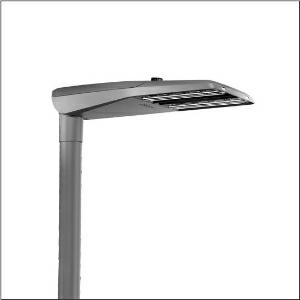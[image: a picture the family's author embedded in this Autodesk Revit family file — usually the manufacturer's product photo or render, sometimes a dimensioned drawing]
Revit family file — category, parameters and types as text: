
# Revit family: streetlight_sl_11_iq_midi___st1_2a_5xc3a41u08le_6743
name_source: partatom
category: Lighting Fixtures
units: mm (PartAtom-declared; Revit-internal decimal feet)

## family parameters
Cut with Voids When Loaded = No
Host = Face
Light Source = No
Part Type = Normal
Room Calculation Point = No
Round Connector Dimension = Use Diameter
Shared = No

## types (1)
- --- (1 x LED, 9590 lm, 59.4 W, 4000K)
    Apparent Load = 59 VA
    CIE Flux Codes = 32 70 96 100 100
    Color Rendering = 70
    Color Temperature = 4000K
    Default Elevation = 1800 mm
    Description = Streetlight SL 11 iQ midi, mast luminaire, primary light control with 3 zone facetted reflector, of plastic, silver coated, highly specular, primary optical cover: cover, of PMMA, transparent, light distribution: ST1.2a, light emission: direct distribution, primary light characteristic: asymmetric, installation type: post-top, side-entry, lamps: LED, High Power LED, rated values: 9.590lm | 59,4W | 161,4lm/W (begin service life); end service life: 9.590lm | 61,6W; at 50% lumin. flux: 4.795lm | 28,5W | 168,2lm/W, colour temperature: 4000K, colour rendering: CRI > 70, light colour: 740, light setting 1 begin service life: 100% | 9.590lm | 59,4W | 161,4lm/W | 4.000K, light setting 1 end service life: 61,6W, further light settings possible, control: pre-setting: logarithmic dimming characteristic, Street-Remote, Auto-Match, Temp-Guard, Lumen-Switch, Night-Set, Smart-Wire, Light-Fading, Desk-Remote (wireless, voltage-free reading and setting of iQ features in the workshop via application-optimized NFC function/RFID function), optimised constant luminous flux control (CLO 2.0), with cable H07RN-F 3x 1.5mm², mains connection: 230..240V, AC, 50/60Hz, connection cable pre-assembled, cable length: 8,5m, luminaire housing, of diecast aluminium, powder-coated, SITECO metallic grey (DB 702S), please order mast flange separately, inclination adjustable without tools: 0°, 5°, 10°, 15° (post-top) | 0°, -5°, -10°, -15° (side-entry), sealing non-destructively replaceable, multi-level sealing system, length: 780mm, width: 376mm, height: 118mm, mast flange for spigot size: 42mm (side-entry): 5XC10008XM4, 60/48mm (side-entry/post-top): 5XC10108XM2, 76/60mm (side-entry/post-top): 5XC10108XM1, equipment: standard, Smart Interface below, protection rating (complete): IP66, insulation class (complete): insulation class II (safety insulation), certification: CE, ENEC, ENEC+, VDE, UKCA, impact resistance: IK10, permissible operating ambient temperature for outdoor applications: -25..+50°C, standard-compliant lighting for roads and squares, Environmental Product Declaration (EPD) tested and certified by an independent institute, packaging unit: 1 piece

Light Distribution: ST1.2a
    Height = 118 mm
    Lamp = 1 x LED
    Lamp Light Flux = 9590 lm
    Lamp Power = 59.4 W
    Lamp count = 1
    Length = 780 mm
    Luminous efficacy = 161 lm/W
    Manufacturer = Siteco
    ModVariant = No
    Model = 5XC3A41U08LE
    Number of Poles = 1
    OnlyDefault = Yes
    Power Factor = 1
    Product Name = Streetlight SL 11 iQ midi | ST1.2a
    Product group = mast luminaire | pylon top
    ProductGroupID = 6100
    Protection Class = Protection class II
    Protection Degree = IP 66
    RLX_Detail_Level = 1
    RLX_Emergency_Light_Flux = 0 lm
    RLX_Emergency_Type = 0
    RLX_Emergency_Type_DB = No
    RlxData = <blob elided: 69993 chars, md5=8f774a45>
    Socket = socket
    Standby Power = 0 W
    System Light Flux = 9590 lm
    System Power = 59 W
    Type Comments = factory setting: luminous flux: 100 % | dim-lin: 254 | 521 mA
    Type Image = l_1005968.jpg
    URL = http://relux.com
    VarID = @adj_132651
    Voltage = 0 V
    Weight = 0.00 kg
    Width = 376 mm

## geometry (parser evidence)
native form markers: Blend x4, Sweep x9
no freeform markers — native parametric forms only
